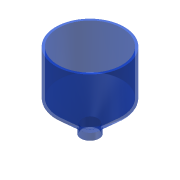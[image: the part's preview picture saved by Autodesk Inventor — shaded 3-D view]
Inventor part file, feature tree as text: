
AUTODESK INVENTOR PART (.ipt)
format: ipt  version: 2014 SP1 (Build 180222100, 222)  size: 136,704 bytes
history: native  units: in
note: dims shown in document units (in); Inventor stores cm internally (conversion verified against a paired STEP export)
features: extrude x5, sketch x5, other x2, loft x1, fillet x1, shell x1
ambient origin geometry x8: Origin, YZ Plane, XZ Plane, XY Plane, X Axis, Y Axis, Z Axis, Center Point
bodies: Solid1 (feature_tree)
feature tree (15):
  extrude  "Extrusion1"  Depth=1.0in TaperAngle=0.0deg
  extrude  "Extrusion2"  Depth=3.0in TaperAngle=0.0deg
  loft  "Loft1"
  fillet  "Fillet1"  Radius=0.125in
  extrude  "Extrusion3"  Depth=0.1in
  shell  "Shell1"  Thickness=0.695in
  extrude  "Extrusion4"  Depth=0.3in TaperAngle=0.0deg
  extrude  "Extrusion5"  [1 undecoded]
  sketch  "Sketch1"  dims[d0=0.795in d1=1.0in d2=0.0in]
  sketch  "Sketch2"  dims[d3=3.0in d4=2.0in d5=0.0in]
  other  "Edges1"
  other  "Edges2"
  sketch  "Sketch3"  dims[d6=0.0in d7=90.0deg d8=0.0in d9=90.0deg d10=0.125in]
  sketch  "Sketch4"  dims[d11=2.0in d12=0.0in d13=0.1in d14=0.695in]
  sketch  "Sketch5"  dims[d15=2.0in d16=0.0in d17=0.3in d18=0.0in]
note: 1 required parameter value undecoded (feature->parameter linkage not recoverable at this tier; creation-order binding heuristic only, values carry confidence <= 0.55)
